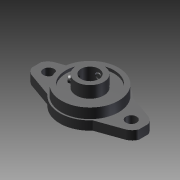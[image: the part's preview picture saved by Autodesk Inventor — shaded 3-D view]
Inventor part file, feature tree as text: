
AUTODESK INVENTOR PART (.ipt)
format: ipt  version: 2016 (Build 200138000, 138)  size: 232,448 bytes
history: native  units: mm
features: sketch x10, other x7, revolve x6, extrude x4
ambient origin geometry x8: Origin, YZ Plane, XZ Plane, XY Plane, X Axis, Y Axis, Z Axis, Center Point
bodies: Solid1 (feature_tree)
feature tree (27):
  extrude  "Extrusion1"  TaperAngle=360.0deg  [1 undecoded]
  revolve  "Revolution1"  Angle=360.0deg
  extrude  "Extrusion2"  TaperAngle=360.0deg  [1 undecoded]
  revolve  "Revolution2"  Angle=360.0deg
  revolve  "Revolution3"  [1 undecoded]
  revolve  "Revolution4"  [1 undecoded]
  revolve  "Revolution5"  [1 undecoded]
  revolve  "Revolution6"  [1 undecoded]
  extrude  "Extrusion3"  [1 undecoded]
  extrude  "Extrusion4"  [1 undecoded]
  other  "housing_XY"
  other  "housing_YZ"
  other  "housing_ZX"
  other  "housing_X"
  other  "housing_Y"
  other  "housing_Z"
  other  "housing_Center"
  sketch  "Sketch_1"  dims[d0=4.0mm d1=0.0mm d2=360.0deg]
  sketch  "Sketch_2"  dims[d3=1.0mm d4=0.0mm d5=360.0deg]
  sketch  "Sketch_5"  dims[d6=360.0deg d7=360.0deg]
  sketch  "Sketch_6"  dims[d8=360.0deg d9=360.0deg]
  sketch  "Sketch_7"  dims[d10=1.5mm d11=0.0mm d12=1.5mm d13=0.0mm]
  sketch  "Sketch_8"  dims[d14=0.0mm]
  sketch  "Sketch_9"
  sketch  "Sketch_10"
  sketch  "Sketch_11"
  sketch  "Sketch_12"
note: 8 required parameter values undecoded (feature->parameter linkage not recoverable at this tier; creation-order binding heuristic only, values carry confidence <= 0.55)